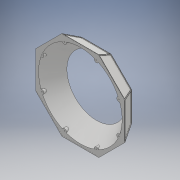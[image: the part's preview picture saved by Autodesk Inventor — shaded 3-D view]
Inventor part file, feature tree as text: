
AUTODESK INVENTOR PART (.ipt)
format: ipt  version: 2017 (Build 210142000, 142)  size: 317,952 bytes
history: native  units: mm
features: sketch x12, extrude x10, projected_geometry x9, draft x2, hole x1
ambient origin geometry x8: Origin, YZ Plane, XZ Plane, XY Plane, X Axis, Y Axis, Z Axis, Center Point
bodies: Solid1 (feature_tree)
feature tree (34):
  extrude  "Extrusion1"  Depth=110.0mm
  draft  "FaceDraft1"
  sketch  "Sketch2"  dims[d2=30.0mm d3=0.0mm d4=30.0deg]
  draft  "FaceDraft2"
  sketch  "Sketch3"  dims[d5=27.0mm d6=27.0mm]
  sketch  "Sketch4"  dims[d7=54.0mm d8=6.457718mm]
  sketch  "Sketch5"  dims[d9=1.0mm d10=1.0mm]
  sketch  "Sketch6"  dims[d11=1.0mm d12=1.0mm]
  sketch  "Sketch7"  dims[d13=1.0mm d14=1.0mm]
  sketch  "Sketch8"  dims[d15=1.0mm d16=1.0mm]
  sketch  "Sketch9"  dims[d17=1.0mm d18=0.0mm d19=1.0mm d20=0.0mm]
  sketch  "Sketch10"  dims[d21=1.0mm d22=0.0mm d23=1.0mm d24=0.0mm]
  extrude  "Extrusion2"  TaperAngle=30.0deg  [1 undecoded]
  extrude  "Extrusion3"  Depth=27.0mm
  extrude  "Extrusion4"  Depth=6.457718mm
  extrude  "Extrusion5"  Depth=1.0mm
  extrude  "Extrusion6"  Depth=1.0mm
  extrude  "Extrusion7"  Depth=1.0mm
  extrude  "Extrusion8"  Depth=1.0mm
  extrude  "Extrusion9"  Depth=1.0mm TaperAngle=0.0deg
  extrude  "Extrusion10"  Depth=1.0mm TaperAngle=0.0deg
  hole  "Hole1"  [1 undecoded]
  sketch  "Sketch1"  dims[d0=150.0mm d1=110.0mm]
  projected_geometry  "Projected Loop1"
  projected_geometry  "Projected Loop2"
  projected_geometry  "Projected Loop3"
  projected_geometry  "Projected Loop4"
  projected_geometry  "Projected Loop5"
  projected_geometry  "Projected Loop6"
  projected_geometry  "Projected Loop7"
  projected_geometry  "Projected Loop8"
  sketch  "Sketch11"  dims[d25=1.0mm d26=0.0mm d27=1.0mm d28=0.0mm]
  sketch  "Sketch12"  dims[d29=1.0mm d30=0.0mm d31=1.0mm d32=0.0mm d35=8.0mm d36=8.0mm d37=8.0mm d38=8.0mm d39=8.0mm d40=8.0mm d41=8.0mm d42=8.0mm d43=5.0mm d44=0.0mm d45=1.5mm d46=6.0mm d47=4.0mm d48=2.0mm d49=90.0deg d50=13.0mm d51=20.594885mm]
  projected_geometry  "Projected Loop10"
note: 2 required parameter values undecoded (feature->parameter linkage not recoverable at this tier; creation-order binding heuristic only, values carry confidence <= 0.55)
